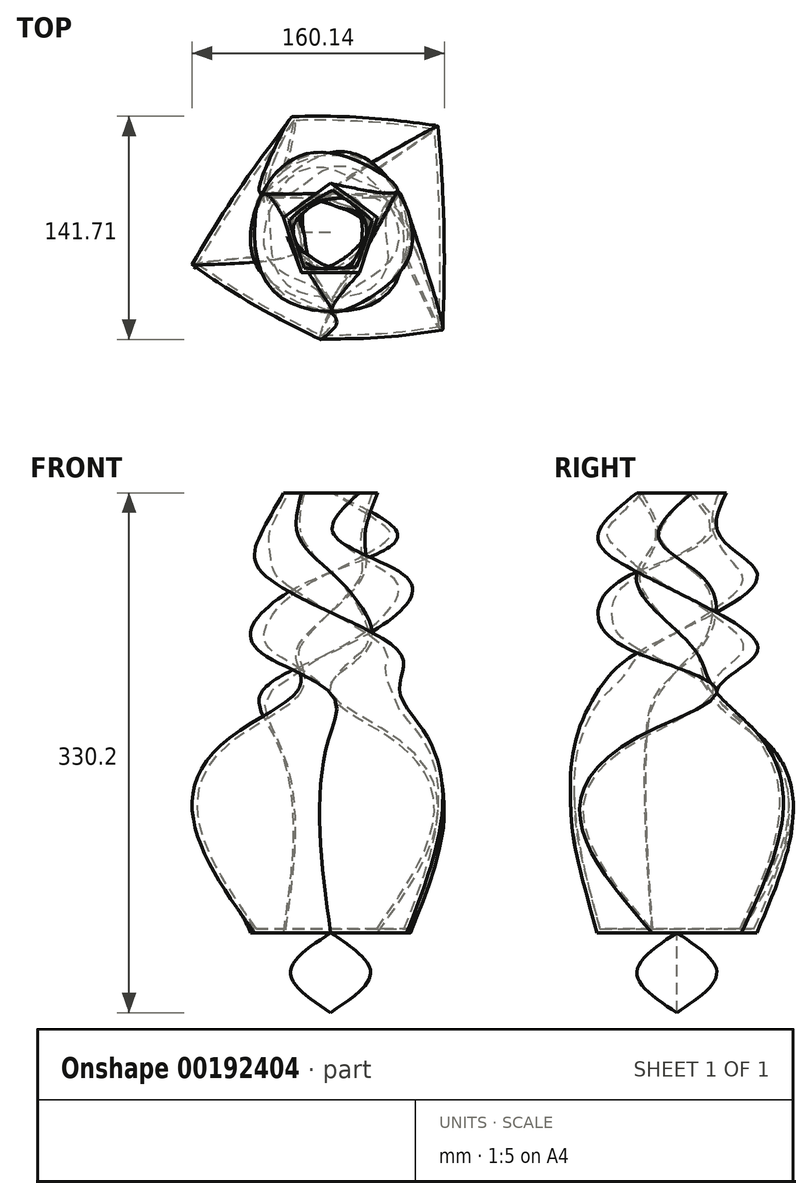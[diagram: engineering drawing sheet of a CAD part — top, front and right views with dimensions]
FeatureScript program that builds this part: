
annotation { "Feature Type Name" : "Feature", "Feature Type Description" : "" }
export const myFeature = defineFeature(function(context is Context, id is Id, definition is map)
    precondition{}
    {
        {
            var Q0;
            Q0=qCreatedBy(makeId("Top.planeOp"),FACE);
            cPlane(context, id + "F0", {"entities" : qUnion([Q0]), "cplaneType" : CPlaneType.OFFSET, "offset" : 25.4 * mm, "width" : 152.4 * mm, "height" : 152.4 * mm});
        }
        {
            var Q0;
            Q0=qCreatedBy(id+"F0.planeOp",FACE);
            cPlane(context, id + "F1", {"entities" : qUnion([Q0]), "cplaneType" : CPlaneType.OFFSET, "offset" : 25.4 * mm, "width" : 152.4 * mm, "height" : 152.4 * mm});
        }
        {
            var Q0;
            Q0=qCreatedBy(id+"F1.planeOp",FACE);
            cPlane(context, id + "F2", {"entities" : qUnion([Q0]), "cplaneType" : CPlaneType.OFFSET, "offset" : 127 * mm, "width" : 152.4 * mm, "height" : 152.4 * mm});
        }
        {
            var Q0;
            Q0=qCreatedBy(id+"F2.planeOp",FACE);
            cPlane(context, id + "F3", {"entities" : qUnion([Q0]), "cplaneType" : CPlaneType.OFFSET, "offset" : 25.4 * mm, "width" : 152.4 * mm, "height" : 152.4 * mm});
        }
        {
            var Q0;
            Q0=qCreatedBy(id+"F3.planeOp",FACE);
            cPlane(context, id + "F4", {"entities" : qUnion([Q0]), "cplaneType" : CPlaneType.OFFSET, "offset" : 25.4 * mm, "width" : 152.4 * mm, "height" : 152.4 * mm});
        }
        {
            var Q0;
            Q0=qCreatedBy(id+"F4.planeOp",FACE);
            cPlane(context, id + "F5", {"entities" : qUnion([Q0]), "cplaneType" : CPlaneType.OFFSET, "offset" : 25.4 * mm, "width" : 152.4 * mm, "height" : 152.4 * mm});
        }
        {
            var Q0;
            Q0=qCreatedBy(id+"F5.planeOp",FACE);
            cPlane(context, id + "F6", {"entities" : qUnion([Q0]), "cplaneType" : CPlaneType.OFFSET, "offset" : 25.4 * mm, "width" : 152.4 * mm, "height" : 152.4 * mm});
        }
        {
            var Q0;
            Q0=qCreatedBy(id+"F6.planeOp",FACE);
            cPlane(context, id + "F7", {"entities" : qUnion([Q0]), "cplaneType" : CPlaneType.OFFSET, "offset" : 25.4 * mm, "width" : 152.4 * mm, "height" : 152.4 * mm});
        }
        {
            var Q0;
            Q0=qCreatedBy(id+"F7.planeOp",FACE);
            cPlane(context, id + "F8", {"entities" : qUnion([Q0]), "cplaneType" : CPlaneType.OFFSET, "offset" : 25.4 * mm, "width" : 152.4 * mm, "height" : 152.4 * mm});
        }
        {
            var Q0;
            Q0=qCreatedBy(id+"F0.planeOp",FACE);
            var sketch = newSketch(context, id + "F9", { "sketchPlane" : qUnion([Q0])});
            skCircle(sketch, "E0", {"center": v(0, 0) * mm, "radius": 25.4 * mm});
            skSolve(sketch);
        }
        {
            var Q0;
            Q0=qCreatedBy(id+"F1.planeOp",FACE);
            var sketch = newSketch(context, id + "F10", { "sketchPlane" : qUnion([Q0])});
            skCircle(sketch, "E1", {"center": v(0, 0) * mm, "radius": 50.8 * mm});
            skSolve(sketch);
        }
        {
            var Q0;
            Q0=qCreatedBy(makeId("Origin.pointOp"),VERTEX);
            var Q1;
            Q1=makeQuery(id+"F9.imprint","IMPRINT",FACE,{"disambiguationData":[TD([[makeQuery(id+"F9.imprint","IMPRINT",EDGE,{"derivedFrom":sQuery(id+"F9.wireOp",EDGE,"E0")}),1.0]])]});
            var Q2;
            Q2=sQuery(id+"F10.wireOp",VERTEX,"E1.center");
            loft(context, id + "F11", {"sheetProfilesArray" : [{ "sheetProfileEntities" : qUnion([Q0]) }, { "sheetProfileEntities" : qUnion([Q1]) }, { "sheetProfileEntities" : qUnion([Q2]) }]});
        }
        {
            var Q0;
            Q0=qCreatedBy(id+"F2.planeOp",FACE);
            var sketch = newSketch(context, id + "F12", { "sketchPlane" : qUnion([Q0])});
            skCircle(sketch, "E2.cCircle", {"center": v(0, 0) * mm, "radius": 50.84 * mm, "construction": true});
            skLineSegment(sketch, "E2.0", {"start": v(-36.94, 50.84) * mm, "end": v(36.94, 50.84) * mm});
            skLineSegment(sketch, "E2.1", {"start": v(36.94, 50.84) * mm, "end": v(59.77, -19.42) * mm});
            skLineSegment(sketch, "E2.2", {"start": v(59.77, -19.42) * mm, "end": v(0, -62.84) * mm});
            skLineSegment(sketch, "E2.3", {"start": v(0, -62.84) * mm, "end": v(-59.77, -19.42) * mm});
            skLineSegment(sketch, "E2.4", {"start": v(-59.77, -19.42) * mm, "end": v(-36.94, 50.84) * mm});
            skPoint(sketch, "E2.0.midPoint", {"position": v(0, 50.84) * mm});
            skSolve(sketch);
        }
        {
            var Q0;
            Q0=qCreatedBy(id+"F3.planeOp",FACE);
            var sketch = newSketch(context, id + "F13", { "sketchPlane" : qUnion([Q0])});
            skCircle(sketch, "E3.cCircle", {"center": v(0, 0) * mm, "radius": 25.42 * mm, "construction": true});
            skLineSegment(sketch, "E3.0", {"start": v(-44.03, 25.42) * mm, "end": v(44.03, 25.42) * mm});
            skLineSegment(sketch, "E3.1", {"start": v(44.03, 25.42) * mm, "end": v(0, -50.84) * mm});
            skLineSegment(sketch, "E3.2", {"start": v(0, -50.84) * mm, "end": v(-44.03, 25.42) * mm});
            skPoint(sketch, "E3.0.midPoint", {"position": v(0, 25.42) * mm});
            skSolve(sketch);
        }
        {
            var Q0;
            Q0=qCreatedBy(id+"F4.planeOp",FACE);
            var sketch = newSketch(context, id + "F14", { "sketchPlane" : qUnion([Q0])});
            skPoint(sketch, "E4.middle", {"position": v(0, 0) * mm});
            skCircle(sketch, "E5.cCircle", {"center": v(0, 0) * mm, "radius": 25.42 * mm, "construction": true});
            skLineSegment(sketch, "E5.0", {"start": v(44.03, -25.42) * mm, "end": v(-44.03, -25.42) * mm});
            skLineSegment(sketch, "E5.1", {"start": v(-44.03, -25.42) * mm, "end": v(0, 50.84) * mm});
            skLineSegment(sketch, "E5.2", {"start": v(0, 50.84) * mm, "end": v(44.03, -25.42) * mm});
            skPoint(sketch, "E5.0.midPoint", {"position": v(0, -25.42) * mm});
            skSolve(sketch);
        }
        {
            var Q0;
            Q0=qCreatedBy(id+"F5.planeOp",FACE);
            var sketch = newSketch(context, id + "F15", { "sketchPlane" : qUnion([Q0])});
            skPoint(sketch, "E6.0.midPoint", {"position": v(1.72, 25.86) * mm});
            skCircle(sketch, "E7.cCircle", {"center": v(0, 0) * mm, "radius": 25.03 * mm, "construction": true});
            skLineSegment(sketch, "E7.0", {"start": v(0.45, -50.06) * mm, "end": v(-43.58, 24.64) * mm});
            skLineSegment(sketch, "E7.1", {"start": v(-43.58, 24.64) * mm, "end": v(43.13, 25.42) * mm});
            skLineSegment(sketch, "E7.2", {"start": v(43.13, 25.42) * mm, "end": v(0.45, -50.06) * mm});
            skPoint(sketch, "E7.0.midPoint", {"position": v(-21.57, -12.7) * mm});
            skSolve(sketch);
        }
        {
            var Q0;
            Q0=qCreatedBy(id+"F6.planeOp",FACE);
            var sketch = newSketch(context, id + "F16", { "sketchPlane" : qUnion([Q0])});
            skCircle(sketch, "E8.cCircle", {"center": v(0, 0) * mm, "radius": 25.45 * mm, "construction": true});
            skLineSegment(sketch, "E8.0", {"start": v(-43.33, -26.71) * mm, "end": v(-1.47, 50.88) * mm});
            skLineSegment(sketch, "E8.1", {"start": v(-1.47, 50.88) * mm, "end": v(44.8, -24.17) * mm});
            skLineSegment(sketch, "E8.2", {"start": v(44.8, -24.17) * mm, "end": v(-43.33, -26.71) * mm});
            skPoint(sketch, "E8.0.midPoint", {"position": v(-22.4, 12.08) * mm});
            skSolve(sketch);
        }
        {
            var Q0;
            Q0=qCreatedBy(id+"F7.planeOp",FACE);
            var sketch = newSketch(context, id + "F17", { "sketchPlane" : qUnion([Q0])});
            skCircle(sketch, "E9.cCircle", {"center": v(0, 0) * mm, "radius": 24.9 * mm, "construction": true});
            skLineSegment(sketch, "E9.0", {"start": v(1.59, -49.76) * mm, "end": v(-43.88, 23.5) * mm});
            skLineSegment(sketch, "E9.1", {"start": v(-43.88, 23.5) * mm, "end": v(42.3, 26.25) * mm});
            skLineSegment(sketch, "E9.2", {"start": v(42.3, 26.25) * mm, "end": v(1.59, -49.76) * mm});
            skPoint(sketch, "E9.0.midPoint", {"position": v(-21.15, -13.13) * mm});
            skSolve(sketch);
        }
        {
            var Q0;
            Q0=qCreatedBy(id+"F8.planeOp",FACE);
            var sketch = newSketch(context, id + "F18", { "sketchPlane" : qUnion([Q0])});
            skCircle(sketch, "E10.cCircle", {"center": v(0, 0) * mm, "radius": 25.42 * mm, "construction": true});
            skLineSegment(sketch, "E10.0", {"start": v(18.47, -25.42) * mm, "end": v(-18.47, -25.42) * mm});
            skLineSegment(sketch, "E10.1", {"start": v(-18.47, -25.42) * mm, "end": v(-29.88, 9.7) * mm});
            skLineSegment(sketch, "E10.2", {"start": v(-29.88, 9.7) * mm, "end": v(0, 31.42) * mm});
            skLineSegment(sketch, "E10.3", {"start": v(0, 31.42) * mm, "end": v(29.88, 9.7) * mm});
            skLineSegment(sketch, "E10.4", {"start": v(29.88, 9.7) * mm, "end": v(18.47, -25.42) * mm});
            skPoint(sketch, "E10.0.midPoint", {"position": v(0, -25.42) * mm});
            skSolve(sketch);
        }
        {
            var Q0;
            Q0=makeQuery(id+"F10.imprint","IMPRINT",FACE,{"disambiguationData":[TD([[makeQuery(id+"F10.imprint","IMPRINT",EDGE,{"derivedFrom":sQuery(id+"F10.wireOp",EDGE,"E1")}),1.0]])]});
            var Q1;
            Q1=makeQuery(id+"F12.imprint","IMPRINT",FACE,{"disambiguationData":[TD([[makeQuery(id+"F12.imprint","IMPRINT",EDGE,{"derivedFrom":sQuery(id+"F12.wireOp",EDGE,"E2.0")}),-1.0]])]});
            var Q2;
            Q2=makeQuery(id+"F13.imprint","IMPRINT",FACE,{"disambiguationData":[TD([[makeQuery(id+"F13.imprint","IMPRINT",EDGE,{"derivedFrom":sQuery(id+"F13.wireOp",EDGE,"E3.0")}),-1.0]])]});
            var Q3;
            Q3=makeQuery(id+"F14.imprint","IMPRINT",FACE,{"disambiguationData":[TD([[makeQuery(id+"F14.imprint","IMPRINT",EDGE,{"derivedFrom":sQuery(id+"F14.wireOp",EDGE,"E5.0")}),-1.0]])]});
            var Q4;
            Q4=makeQuery(id+"F15.imprint","IMPRINT",FACE,{"disambiguationData":[TD([[makeQuery(id+"F15.imprint","IMPRINT",EDGE,{"derivedFrom":sQuery(id+"F15.wireOp",EDGE,"E7.0")}),-1.0]])]});
            var Q5;
            Q5=makeQuery(id+"F16.imprint","IMPRINT",FACE,{"disambiguationData":[TD([[makeQuery(id+"F16.imprint","IMPRINT",EDGE,{"derivedFrom":sQuery(id+"F16.wireOp",EDGE,"E8.0")}),-1.0]])]});
            var Q6;
            Q6=makeQuery(id+"F17.imprint","IMPRINT",FACE,{"disambiguationData":[TD([[makeQuery(id+"F17.imprint","IMPRINT",EDGE,{"derivedFrom":sQuery(id+"F17.wireOp",EDGE,"E9.0")}),-1.0]])]});
            var Q7;
            Q7=makeQuery(id+"F18.imprint","IMPRINT",FACE,{"disambiguationData":[TD([[makeQuery(id+"F18.imprint","IMPRINT",EDGE,{"derivedFrom":sQuery(id+"F18.wireOp",EDGE,"E10.0")}),-1.0]])]});
            loft(context, id + "F19", {"sheetProfilesArray" : [{ "sheetProfileEntities" : qUnion([Q0]) }, { "sheetProfileEntities" : qUnion([Q1]) }, { "sheetProfileEntities" : qUnion([Q2]) }, { "sheetProfileEntities" : qUnion([Q3]) }, { "sheetProfileEntities" : qUnion([Q4]) }, { "sheetProfileEntities" : qUnion([Q5]) }, { "sheetProfileEntities" : qUnion([Q6]) }, { "sheetProfileEntities" : qUnion([Q7]) }]});
        }
        {
            var Q0;
            Q0=makeQuery(id+"F19.opLoft","CAP_FACE",FACE,{"disambiguationData":[OSD([makeQuery(id+"F18.imprint","IMPRINT",FACE,{"disambiguationData":[TD([[makeQuery(id+"F18.imprint","IMPRINT",EDGE,{"derivedFrom":sQuery(id+"F18.wireOp",EDGE,"E10.0")}),-1.0]])]})])],"isStart":true});
            shell(context, id + "F20", {"entities" : qUnion([Q0]), "thickness" : 2.54 * mm});
        }
    });
